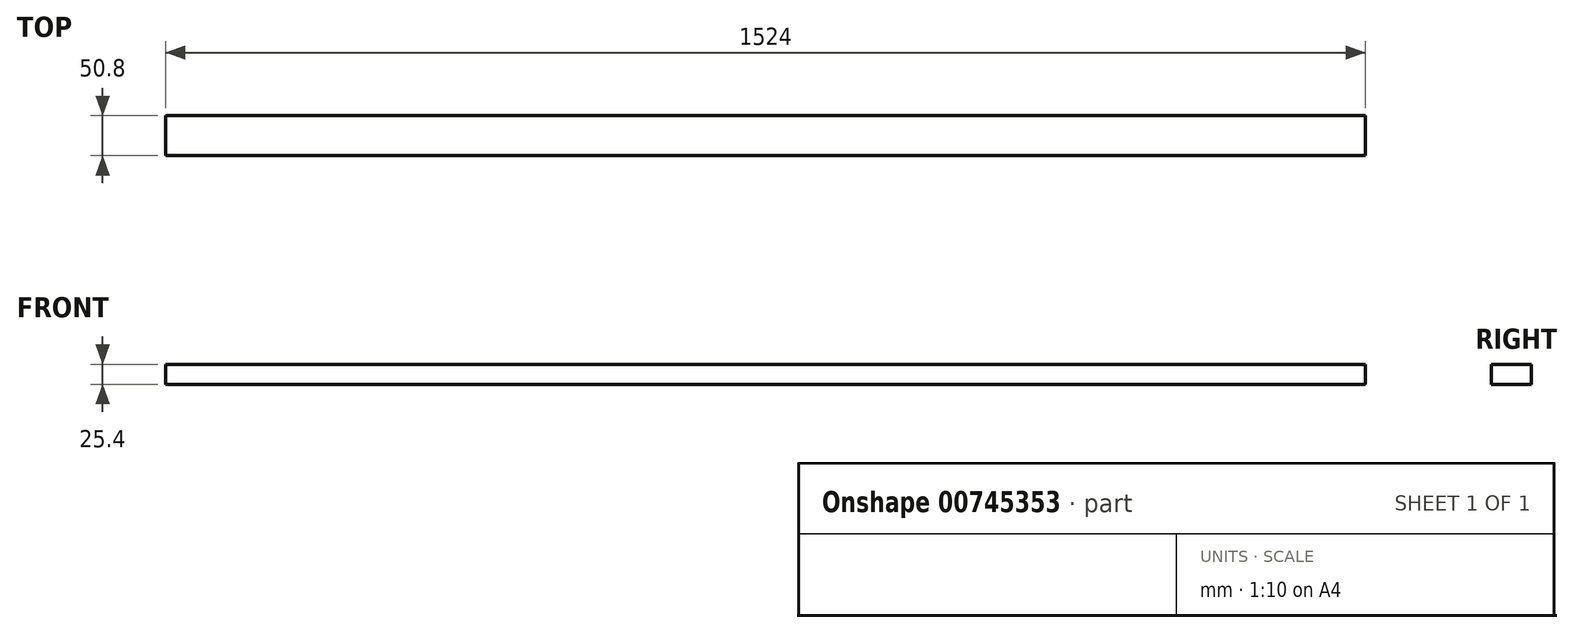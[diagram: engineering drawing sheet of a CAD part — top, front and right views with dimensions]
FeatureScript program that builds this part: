
annotation { "Feature Type Name" : "Feature", "Feature Type Description" : "" }
export const myFeature = defineFeature(function(context is Context, id is Id, definition is map)
    precondition{}
    {
        {
            var Q0;
            Q0=qCreatedBy(makeId("Top.planeOp"),FACE);
            var sketch = newSketch(context, id + "F0", { "sketchPlane" : qUnion([Q0])});
            skLineSegment(sketch, "E0.bottom", {"start": v(0, 0) * mm, "end": v(1524, 0) * mm});
            skLineSegment(sketch, "E0.top", {"start": v(0, 50.8) * mm, "end": v(1524, 50.8) * mm});
            skLineSegment(sketch, "E0.left", {"start": v(0, 0) * mm, "end": v(0, 50.8) * mm});
            skLineSegment(sketch, "E0.right", {"start": v(1524, 0) * mm, "end": v(1524, 50.8) * mm});
            skSolve(sketch);
        }
        {
            var Q0;
            Q0=makeQuery(id+"F0.imprint","IMPRINT",FACE,{"disambiguationData":[TD([[makeQuery(id+"F0.imprint","IMPRINT",EDGE,{"derivedFrom":sQuery(id+"F0.wireOp",EDGE,"XOJL2qkw-726g-F02Q-CQMI-GWsZiQ8f43vg.bottom")}),1.0]])]});
            var Q1;
            Q1=makeQuery(id+"F0.imprint","IMPRINT",FACE,{"disambiguationData":[TD([[makeQuery(id+"F0.imprint","IMPRINT",EDGE,{"derivedFrom":sQuery(id+"F0.wireOp",EDGE,"E0.bottom")}),1.0]])]});
            extrude(context, id + "F1", {"entities" : qUnion([Q0, Q1]), "depth" : 25.4 * mm, "offsetDistance" : 25.4 * mm});
        }
    });
